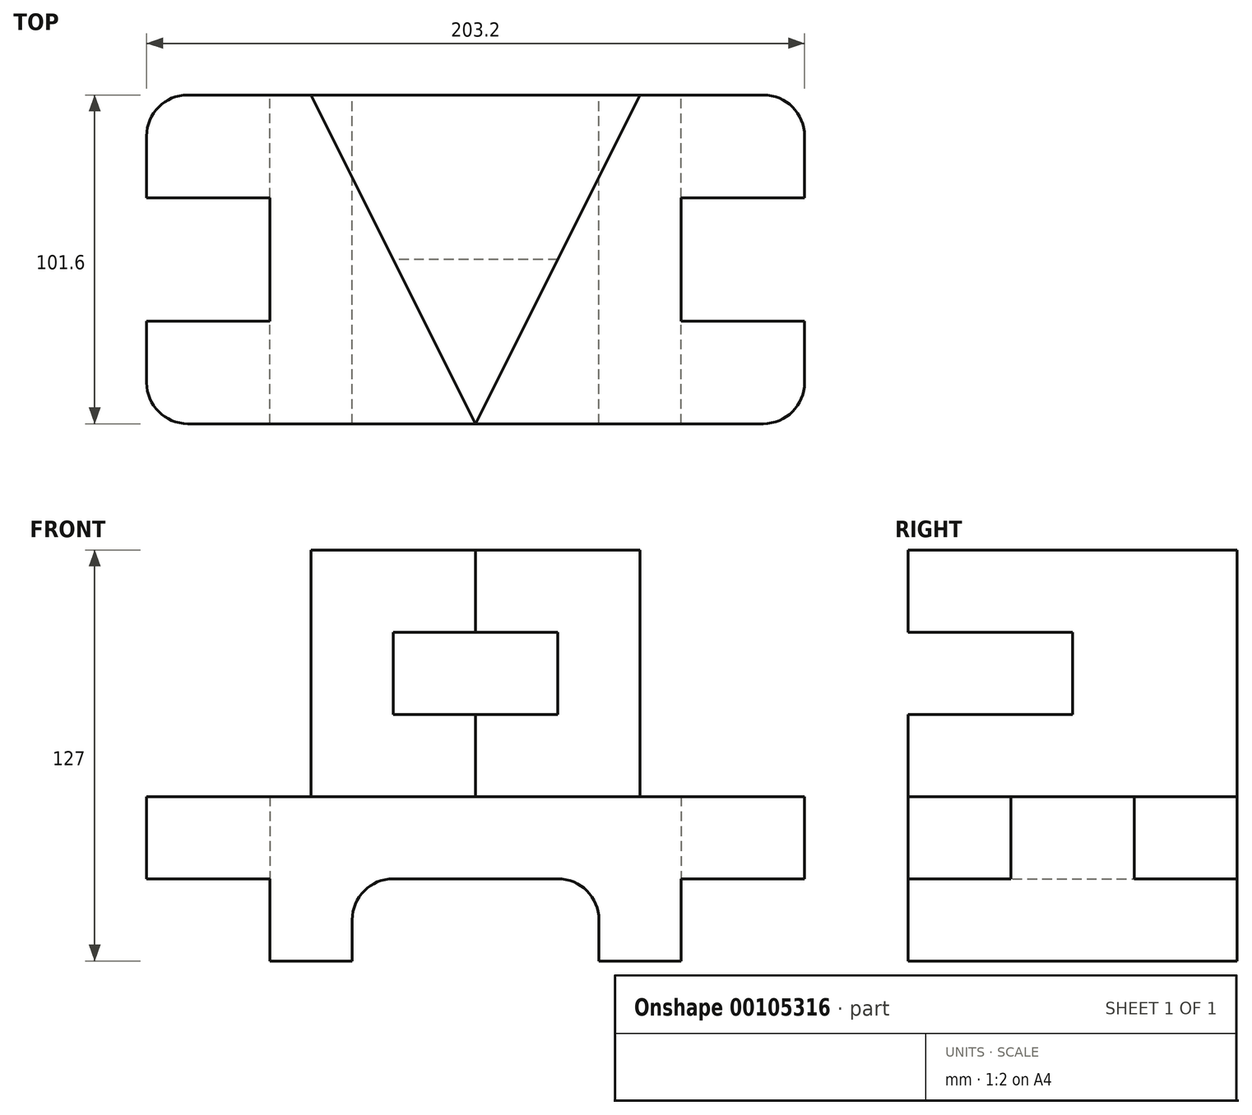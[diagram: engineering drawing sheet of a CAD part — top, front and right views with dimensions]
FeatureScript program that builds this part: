
annotation { "Feature Type Name" : "Feature", "Feature Type Description" : "" }
export const myFeature = defineFeature(function(context is Context, id is Id, definition is map)
    precondition{}
    {
        {
            var Q0;
            Q0=qCreatedBy(makeId("Front.planeOp"),FACE);
            var sketch = newSketch(context, id + "F0", { "sketchPlane" : qUnion([Q0])});
            skLineSegment(sketch, "E0", {"start": v(-101.6, 50.8) * mm, "end": v(101.6, 50.8) * mm});
            skLineSegment(sketch, "E1", {"start": v(101.6, 50.8) * mm, "end": v(101.6, 25.4) * mm});
            skLineSegment(sketch, "E2", {"start": v(101.6, 25.4) * mm, "end": v(63.5, 25.4) * mm});
            skLineSegment(sketch, "E3", {"start": v(63.5, 25.4) * mm, "end": v(63.5, 0) * mm});
            skLineSegment(sketch, "E4", {"start": v(63.5, 0) * mm, "end": v(38.1, 0) * mm});
            skLineSegment(sketch, "E5", {"start": v(38.1, 0) * mm, "end": v(38.1, 25.4) * mm});
            skLineSegment(sketch, "E6", {"start": v(38.1, 25.4) * mm, "end": v(-38.1, 25.4) * mm});
            skLineSegment(sketch, "E7", {"start": v(-38.1, 25.4) * mm, "end": v(-38.1, 0) * mm});
            skLineSegment(sketch, "E8", {"start": v(-38.1, 0) * mm, "end": v(-63.5, 0) * mm});
            skLineSegment(sketch, "E9", {"start": v(-63.5, 0) * mm, "end": v(-63.5, 25.4) * mm});
            skLineSegment(sketch, "E10", {"start": v(-63.5, 25.4) * mm, "end": v(-101.6, 25.4) * mm});
            skLineSegment(sketch, "E11", {"start": v(-101.6, 25.4) * mm, "end": v(-101.6, 50.8) * mm});
            skSolve(sketch);
        }
        {
            var Q0;
            Q0 = qSketchRegion(id + "F0", true);
            extrude(context, id + "F1", {"entities" : qUnion([Q0]), "endBound" : BoundingType.SYMMETRIC, "depth" : 101.6 * mm});
        }
        {
            var Q0;
            Q0=qCreatedBy(makeId("Front.planeOp"),FACE);
            var sketch = newSketch(context, id + "F2", { "sketchPlane" : qUnion([Q0])});
            skLineSegment(sketch, "E12", {"start": v(-101.6, 50.8) * mm, "end": v(-63.5, 50.8) * mm});
            skLineSegment(sketch, "E13", {"start": v(-63.5, 50.8) * mm, "end": v(-63.5, 25.4) * mm});
            skLineSegment(sketch, "E14", {"start": v(-63.5, 25.4) * mm, "end": v(-101.6, 25.4) * mm});
            skLineSegment(sketch, "E15", {"start": v(-101.6, 25.4) * mm, "end": v(-101.6, 50.8) * mm});
            skLineSegment(sketch, "E16", {"start": v(63.5, 25.4) * mm, "end": v(101.6, 25.4) * mm});
            skLineSegment(sketch, "E17", {"start": v(101.6, 25.4) * mm, "end": v(101.6, 50.8) * mm});
            skLineSegment(sketch, "E18", {"start": v(101.6, 50.8) * mm, "end": v(63.5, 50.8) * mm});
            skLineSegment(sketch, "E19", {"start": v(63.5, 50.8) * mm, "end": v(63.5, 25.4) * mm});
            skSolve(sketch);
        }
        {
            var Q0;
            Q0 = qSketchRegion(id + "F2", true);
            extrude(context, id + "F3", {"entities" : qUnion([Q0]), "operationType" : NewBodyOperationType.REMOVE, "endBound" : BoundingType.SYMMETRIC, "depth" : 38.1 * mm});
        }
        {
            var Q0;
            Q0=makeQuery(id+"F1.opExtrude","CAP_EDGE",EDGE,{"disambiguationData":[OSD([sQuery(id+"F0.wireOp",EDGE,"E1")])],"isStart":false});
            var Q1;
            Q1=makeQuery(id+"F1.opExtrude","CAP_EDGE",EDGE,{"disambiguationData":[OSD([sQuery(id+"F0.wireOp",EDGE,"E1")])],"isStart":true});
            var Q2;
            Q2=makeQuery(id+"F1.opExtrude","CAP_EDGE",EDGE,{"disambiguationData":[OSD([sQuery(id+"F0.wireOp",EDGE,"E11")])],"isStart":false});
            var Q3;
            Q3=makeQuery(id+"F1.opExtrude","CAP_EDGE",EDGE,{"disambiguationData":[OSD([sQuery(id+"F0.wireOp",EDGE,"E11")])],"isStart":true});
            fillet(context, id + "F4", {"entities" : qUnion([Q0, Q1, Q2, Q3]), "radius" : 12.7 * mm, "tangentPropagation" : true, "allowEdgeOverflow" : false});
        }
        {
            var Q0;
            Q0=makeQuery(id+"F1.opExtrude","SWEPT_EDGE",EDGE,{"disambiguationData":[OSD([sQuery(id+"F0.wireOp",EDGE,"E5"),sQuery(id+"F0.wireOp",EDGE,"E6")])]});
            var Q1;
            Q1=makeQuery(id+"F1.opExtrude","SWEPT_EDGE",EDGE,{"disambiguationData":[OSD([sQuery(id+"F0.wireOp",EDGE,"E6"),sQuery(id+"F0.wireOp",EDGE,"E7")])]});
            fillet(context, id + "F5", {"entities" : qUnion([Q0, Q1]), "radius" : 12.7 * mm, "tangentPropagation" : true, "allowEdgeOverflow" : false});
        }
        {
            var Q0;
            Q0=makeQuery(id+"F1.opExtrude","SWEPT_FACE",FACE,{"disambiguationData":[OSD([sQuery(id+"F0.wireOp",EDGE,"E0")])]});
            var sketch = newSketch(context, id + "F6", { "sketchPlane" : qUnion([Q0])});
            skLineSegment(sketch, "E20", {"start": v(0, -50.8) * mm, "end": v(50.8, 50.8) * mm});
            skLineSegment(sketch, "E21", {"start": v(50.8, 50.8) * mm, "end": v(-50.8, 50.8) * mm});
            skLineSegment(sketch, "E22", {"start": v(-50.8, 50.8) * mm, "end": v(0, -50.8) * mm});
            skSolve(sketch);
        }
        {
            var Q0;
            Q0 = qSketchRegion(id + "F6", true);
            extrude(context, id + "F7", {"entities" : qUnion([Q0]), "operationType" : NewBodyOperationType.ADD, "depth" : 76.2 * mm});
        }
        {
            var Q0;
            Q0=qCreatedBy(makeId("Right.planeOp"),FACE);
            var sketch = newSketch(context, id + "F8", { "sketchPlane" : qUnion([Q0])});
            skLineSegment(sketch, "E23", {"start": v(0, 0) * mm, "end": v(0, 76.2) * mm, "construction": true});
            skLineSegment(sketch, "E24", {"start": v(0, 76.2) * mm, "end": v(0, 101.6) * mm});
            skLineSegment(sketch, "E25", {"start": v(0, 101.6) * mm, "end": v(-50.8, 101.6) * mm});
            skLineSegment(sketch, "E26", {"start": v(-50.8, 101.6) * mm, "end": v(-50.8, 76.2) * mm});
            skLineSegment(sketch, "E27", {"start": v(-50.8, 76.2) * mm, "end": v(0, 76.2) * mm});
            skSolve(sketch);
        }
        {
            var Q0;
            Q0 = qSketchRegion(id + "F8", true);
            extrude(context, id + "F9", {"entities" : qUnion([Q0]), "operationType" : NewBodyOperationType.REMOVE, "endBound" : BoundingType.SYMMETRIC, "depth" : 50.8 * mm});
        }
    });
